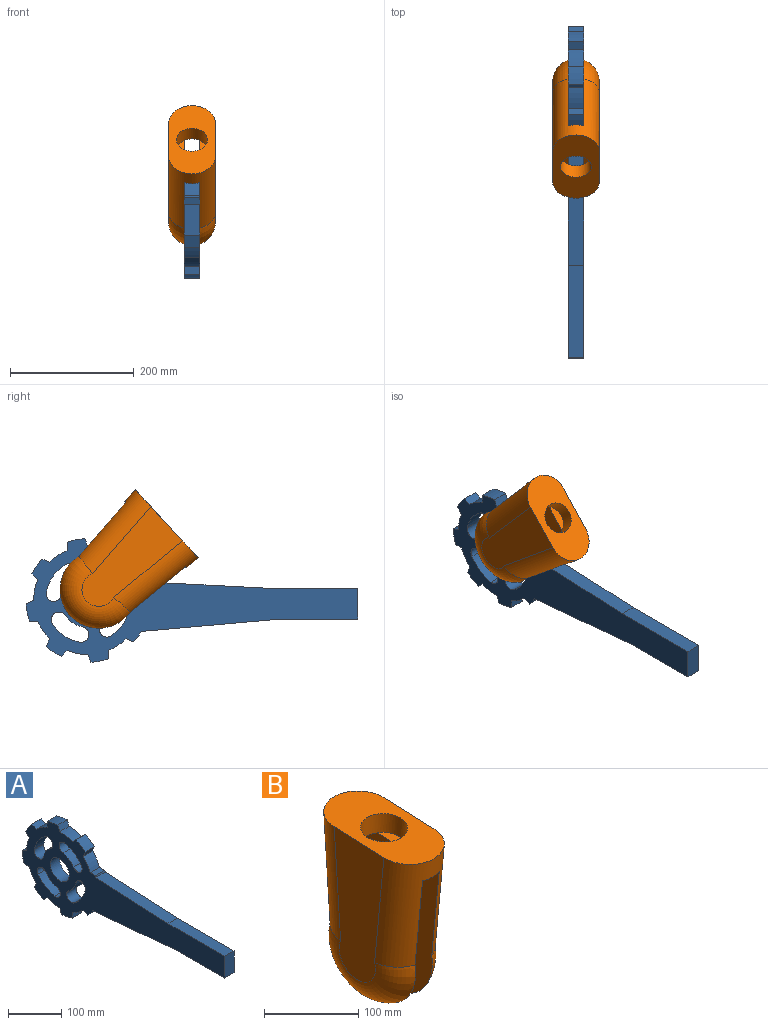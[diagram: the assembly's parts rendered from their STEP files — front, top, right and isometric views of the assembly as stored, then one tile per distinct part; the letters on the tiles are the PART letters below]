
ASSEMBLY  parts=2 mates=1
PART A: 53 faces, bbox 25x536.5x199.7 mm
  f0: plane 536.47x199.74mm, normal (1,0,0), area 39394.4mm2, adj f2,f3,f4,f5,f6,f7,f8,f9
  f1: plane 536.47x199.74mm, normal (-1,0,0), area 39394.4mm2, adj f2,f3,f4,f5,f6,f7,f8,f9
  f2: cylinder r=87.5mm len=28.39mm, axis (-1,0,0), area 859mm2, adj f0,f1,f3,f35
  f3: plane 25x13.39mm, normal (0,0,1), area 334.7mm2, adj f0,f1,f2,f4
  f4: cylinder r=100mm len=25mm, axis (-1,0,0), area 91.9mm2, adj f0,f1,f3,f5
  f5: plane 191.21x25mm, normal (0,-0.05,1), area 4786.7mm2, adj f0,f1,f4,f6
  f6: plane 150x25mm, normal (0,0,1), area 3750mm2, adj f0,f1,f5,f7
  f7: plane 50x25mm, normal (0,-1,0), area 1250mm2, adj f0,f1,f6,f8
  f8: plane 125x25mm, normal (0,0,-1), area 3125mm2, adj f0,f1,f7,f9
  f9: plane 225x25mm, normal (0,-0.09,-1), area 5647.2mm2, adj f0,f1,f8,f10
  f10: cylinder r=100mm len=25mm, axis (-1,0,0), area 526.4mm2, adj f0,f1,f9,f11
  f11: plane 25x12.37mm, normal (0,0.38,-0.92), area 334.7mm2, adj f0,f1,f10,f12
  f12: cylinder r=87.5mm len=28.39mm, axis (-1,0,0), area 859mm2, adj f0,f1,f11,f13
  f13: plane 25x13.39mm, normal (0,-1,0), area 334.7mm2, adj f0,f1,f12,f14
  f14: cylinder r=100mm len=28.36mm, axis (-1,0,0), area 725.5mm2, adj f0,f1,f13,f15
  f15: plane 25x12.37mm, normal (0,0.92,-0.38), area 334.7mm2, adj f0,f1,f14,f16
  f16: cylinder r=87.5mm len=33.49mm, axis (-1,0,0), area 859mm2, adj f0,f1,f15,f17
  f17: plane 25x9.47mm, normal (0,-0.71,-0.71), area 334.7mm2, adj f0,f1,f16,f18
  f18: cylinder r=100mm len=25mm, axis (-1,0,0), area 725.5mm2, adj f0,f1,f17,f19
  f19: plane 25x12.37mm, normal (0,0.92,0.38), area 334.7mm2, adj f0,f1,f18,f20
  f20: cylinder r=87.5mm len=28.39mm, axis (-1,0,0), area 859mm2, adj f0,f1,f19,f21
  f21: plane 25x13.39mm, normal (0,0,-1), area 334.7mm2, adj f0,f1,f20,f22
  f22: cylinder r=100mm len=28.36mm, axis (-1,0,0), area 725.5mm2, adj f0,f1,f21,f23
  f23: plane 25x12.37mm, normal (0,0.38,0.92), area 334.7mm2, adj f0,f1,f22,f24
  f24: cylinder r=87.5mm len=33.49mm, axis (-1,0,0), area 859mm2, adj f0,f1,f23,f25
  f25: plane 25x9.47mm, normal (0,0.71,-0.71), area 334.7mm2, adj f0,f1,f24,f26
  f26: cylinder r=100mm len=25mm, axis (-1,0,0), area 725.5mm2, adj f0,f1,f25,f27
  f27: plane 25x12.37mm, normal (0,-0.38,0.92), area 334.7mm2, adj f0,f1,f26,f28
  f28: cylinder r=87.5mm len=28.39mm, axis (-1,0,0), area 859mm2, adj f0,f1,f27,f29
  f29: plane 25x13.39mm, normal (0,1,0), area 334.7mm2, adj f0,f1,f28,f30
  f30: cylinder r=100mm len=28.36mm, axis (-1,0,0), area 725.5mm2, adj f0,f1,f29,f31
  f31: plane 25x12.37mm, normal (0,-0.92,0.38), area 334.7mm2, adj f0,f1,f30,f32
  f32: cylinder r=87.5mm len=33.49mm, axis (-1,0,0), area 859mm2, adj f0,f1,f31,f33
  f33: plane 25x9.47mm, normal (0,0.71,0.71), area 334.7mm2, adj f0,f1,f32,f34
  f34: cylinder r=100mm len=25mm, axis (-1,0,0), area 725.5mm2, adj f0,f1,f33,f35
  f35: plane 25x12.37mm, normal (0,-0.92,-0.38), area 334.7mm2, adj f0,f1,f2,f34
  f36: cylinder r=25mm len=50mm, axis (-1,0,0), area 3927mm2, adj f0,f1
  f37: cylinder r=43.62mm len=27.76mm, axis (1,0,0), area 856.6mm2, adj f0,f1,f38,f40
  f38: cylinder r=12.5mm len=25mm, axis (1,0,0), area 981.7mm2, adj f0,f1,f37,f39
  f39: cylinder r=68.62mm len=43.67mm, axis (1,0,0), area 1347.4mm2, adj f0,f1,f38,f40
  f40: cylinder r=12.5mm len=25mm, axis (1,0,0), area 981.7mm2, adj f0,f1,f37,f39
  f41: cylinder r=12.5mm len=25mm, axis (1,0,0), area 981.7mm2, adj f0,f1,f42,f44
  f42: cylinder r=43.62mm len=27.76mm, axis (1,0,0), area 856.6mm2, adj f0,f1,f41,f43
  f43: cylinder r=12.5mm len=25mm, axis (1,0,0), area 981.7mm2, adj f0,f1,f42,f44
  f44: cylinder r=68.62mm len=43.67mm, axis (1,0,0), area 1347.4mm2, adj f0,f1,f41,f43
  f45: cylinder r=43.62mm len=27.76mm, axis (1,0,0), area 856.6mm2, adj f0,f1,f46,f48
  f46: cylinder r=12.5mm len=25mm, axis (1,0,0), area 981.7mm2, adj f0,f1,f45,f47
  f47: cylinder r=68.62mm len=43.67mm, axis (1,0,0), area 1347.4mm2, adj f0,f1,f46,f48
  f48: cylinder r=12.5mm len=25mm, axis (1,0,0), area 981.7mm2, adj f0,f1,f45,f47
  f49: cylinder r=12.5mm len=25mm, axis (1,0,0), area 981.7mm2, adj f0,f1,f50,f52
  f50: cylinder r=43.62mm len=27.76mm, axis (1,0,0), area 856.6mm2, adj f0,f1,f49,f51
  f51: cylinder r=12.5mm len=25mm, axis (1,0,0), area 981.7mm2, adj f0,f1,f50,f52
  f52: cylinder r=68.62mm len=43.67mm, axis (1,0,0), area 1347.4mm2, adj f0,f1,f49,f51
PART B: 15 faces, bbox 75x149.9x220.8 mm
  f0: plane 50.63x25mm, normal (0,0.04,-1), area 1192.2mm2, adj f1,f6,f10,f13
  f1: plane 193.05x141.43mm, normal (-1,0,0), area 20940.1mm2, adj f0,f4,f5,f8,f9,f10,f12
  f2: plane 149.89x75mm, normal (0,-0.04,1), area 8074.9mm2, adj f3,f7,f9,f10,f13
  f3: plane 181.41x74.66mm, normal (1,0,0), area 10663.8mm2, adj f2,f8,f9,f10
  f4: cylinder r=25mm len=50mm, axis (1,0,0), area 3927mm2, adj f1,f6
  f5: plane 51.84x25mm, normal (0,0.04,-1), area 1222.7mm2, adj f1,f6,f9,f13
  f6: plane 193.05x141.43mm, normal (1,0,0), area 20940.1mm2, adj f0,f4,f5,f9,f10,f11,f14
  f7: plane 181.41x74.66mm, normal (-1,0,0), area 10663.8mm2, adj f2,f9,f10,f11
  f8: torus R=27.14mm, axis (-1,0,0), area 7953.6mm2, adj f1,f3,f9,f10
  f9: cylinder r=37.5mm len=149.12mm, axis (0,-0.1,1), area 13722.3mm2, adj f1,f2,f3,f5,f6,f7,f8,f11
  f10: cylinder r=37.5mm len=150.13mm, axis (0,-0.07,-1), area 13748mm2, adj f0,f1,f2,f3,f6,f7,f8,f11
  f11: torus R=27.14mm, axis (1,0,0), area 7953.6mm2, adj f6,f7,f9,f10
  f12: plane 43.27x12.5mm, normal (0,-0.04,1), area 383.9mm2, adj f1,f13
  f13: cylinder r=25mm len=50.93mm, axis (0,-0.04,1), area 3927mm2, adj f0,f2,f5,f12,f14
  f14: plane 43.27x12.5mm, normal (0,-0.04,1), area 383.9mm2, adj f6,f13
PLACE A at identity fixed
PLACE B rot(axis=(1,0,0),45deg) t=(0,100,-41.42)mm
MATE revolute A.f2 <-> B.f4  axis (1,0,0) through (12.5,100,100)mm
